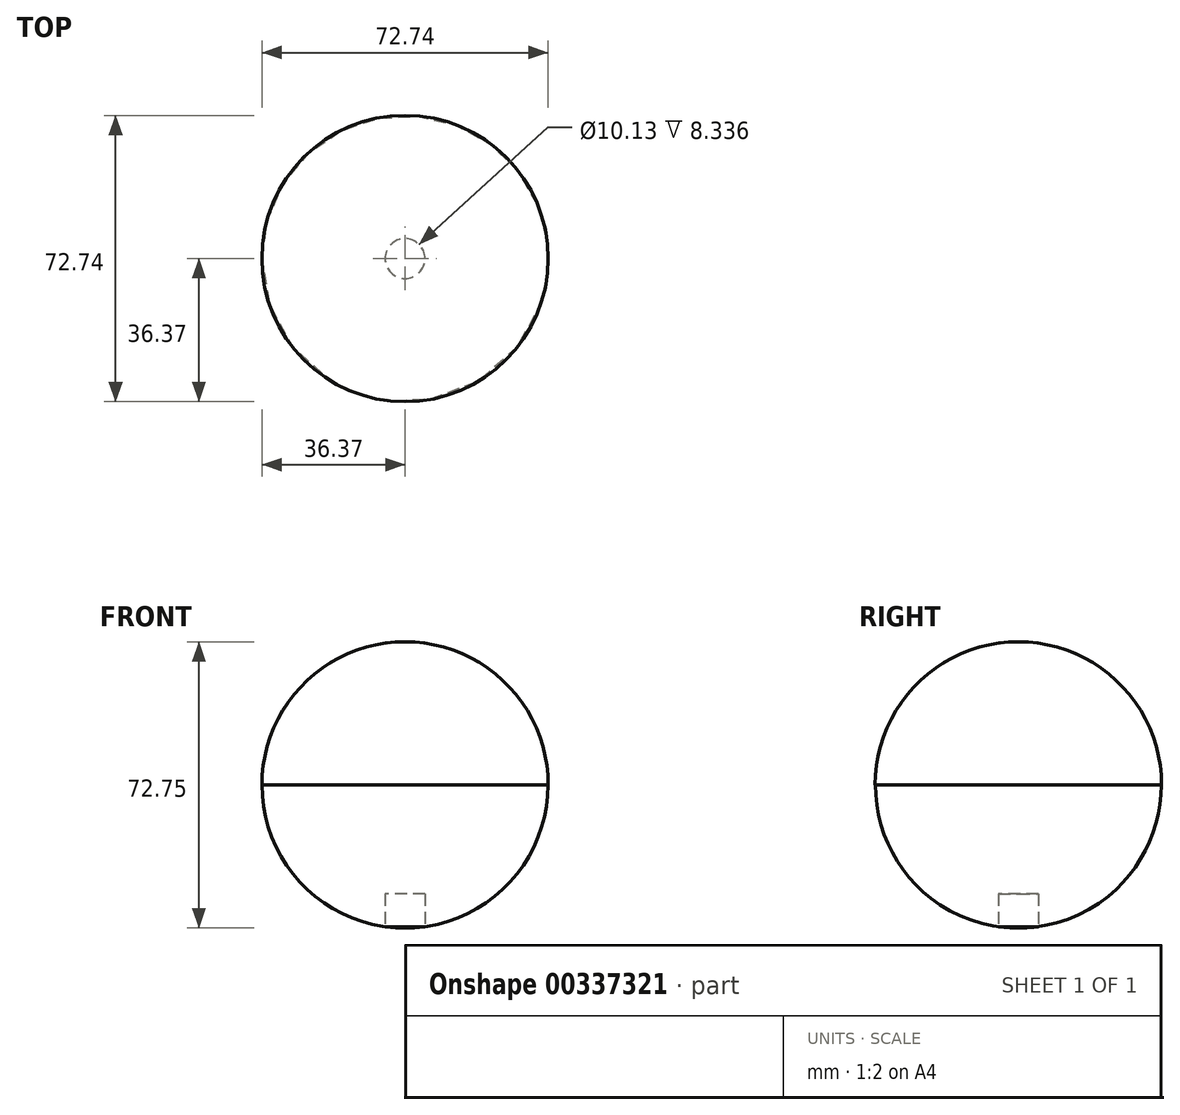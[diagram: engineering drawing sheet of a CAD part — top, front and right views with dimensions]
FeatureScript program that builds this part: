
annotation { "Feature Type Name" : "Feature", "Feature Type Description" : "" }
export const myFeature = defineFeature(function(context is Context, id is Id, definition is map)
    precondition{}
    {
        {
            var Q0;
            Q0=qCreatedBy(makeId("Top.planeOp"),FACE);
            var sketch = newSketch(context, id + "F0", { "sketchPlane" : qUnion([Q0])});
            skCircle(sketch, "E0", {"center": v(0, 0) * mm, "radius": 36.37 * mm});
            skSolve(sketch);
        }
        {
            var Q0;
            Q0 = qSketchRegion(id + "F0", true);
            extrude(context, id + "F1", {"entities" : qUnion([Q0]), "depth" : 72.75 * mm});
        }
        {
            var Q0;
            Q0=makeQuery(id+"F1.opExtrude","CAP_EDGE",EDGE,{"disambiguationData":[OSD([sQuery(id+"F0.wireOp",EDGE,"E0")])],"isStart":false});
            fillet(context, id + "F2", {"entities" : qUnion([Q0]), "radius" : 36.35 * mm, "tangentPropagation" : true, "allowEdgeOverflow" : false});
        }
        {
            var Q0;
            Q0=makeQuery(id+"F1.opExtrude","CAP_FACE",FACE,{"disambiguationData":[OSD([sQuery(id+"F0.wireOp",EDGE,"E0")])],"isStart":true});
            var Q1;
            {var subQ0=sQuery(id+"F0.wireOp",EDGE,"E0");Q1=makeQuery(id+"F2.opFillet","BLEND_EDGE",EDGE,{"blendedFrom":[makeQuery(id+"F1.opExtrude","CAP_EDGE",EDGE,{"disambiguationData":[OSD([subQ0])],"isStart":false}),makeQuery(id+"F1.opExtrude","SWEPT_FACE",FACE,{"disambiguationData":[OSD([subQ0])]})],"blendedInto":[makeQuery(id+"F1.opExtrude","SWEPT_FACE",FACE,{"disambiguationData":[OSD([subQ0])]})]});}
            fillet(context, id + "F3", {"entities" : qUnion([Q0, Q1]), "radius" : 36.35 * mm, "tangentPropagation" : true, "allowEdgeOverflow" : false});
        }
        {
            var Q0;
            Q0=qCreatedBy(makeId("Top.planeOp"),FACE);
            var sketch = newSketch(context, id + "F4", { "sketchPlane" : qUnion([Q0])});
            skCircle(sketch, "E1", {"center": v(0, 0) * mm, "radius": 5.07 * mm});
            skSolve(sketch);
        }
        {
            var Q0;
            Q0 = qSketchRegion(id + "F4", true);
            extrude(context, id + "F5", {"entities" : qUnion([Q0]), "operationType" : NewBodyOperationType.REMOVE, "depth" : 8.7 * mm});
        }
    });
